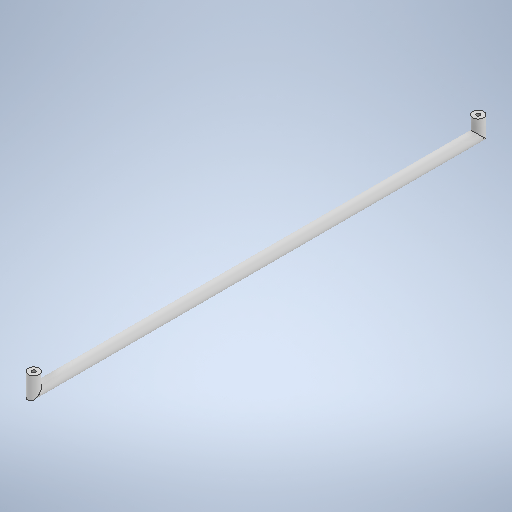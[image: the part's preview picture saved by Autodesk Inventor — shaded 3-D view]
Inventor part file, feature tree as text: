
AUTODESK INVENTOR PART (.ipt)
format: ipt  version: 2025 (Build 290162010, 162A)  size: 297,984 bytes
history: native  units: in
note: dims shown in document units (in); Inventor stores cm internally (conversion verified against a paired STEP export)
features: sketch x4, extrude x3, hole x1
ambient origin geometry x8: Origin, YZ Plane, XZ Plane, XY Plane, X Axis, Y Axis, Z Axis, Center Point
bodies: Solid1 (feature_tree)
feature tree (8):
  extrude  "Extrusion1"  Depth=10.1969in TaperAngle=0.0deg
  extrude  "Extrusion2"  Depth=5.1132in
  hole  "Hole1"  [1 undecoded]
  extrude  "Extrusion5"  TaperAngle=0.0deg  [1 undecoded]
  sketch  "Sketch1"  dims[d0=0.25in d1=10.1969in d2=0.0in]
  sketch  "Sketch2"  dims[d4=10.2264in d5=5.1132in]
  sketch  "Sketch3"  dims[d6=0.25in d7=0.25in]
  sketch  "Sketch6"  dims[d8=0.3937in d9=0.125in d10=0.0in d11=0.0in d12=0.0849in d13=0.224in d14=0.325in d15=0.25in d16=0.5635in d17=1.0in d18=0.0in d23=0.0in d24=0.0in]
note: 2 required parameter values undecoded (feature->parameter linkage not recoverable at this tier; creation-order binding heuristic only, values carry confidence <= 0.55)
